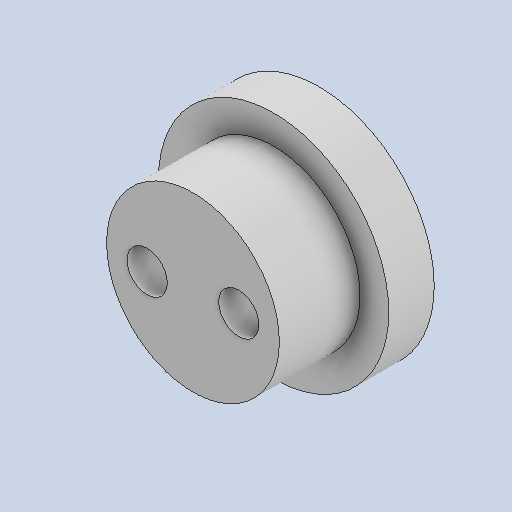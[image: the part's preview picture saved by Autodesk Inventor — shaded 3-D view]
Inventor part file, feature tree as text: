
AUTODESK INVENTOR PART (.ipt)
format: ipt  version: 2023 (Build 270158000, 158)  size: 157,696 bytes
history: native  units: in
note: dims shown in document units (in); Inventor stores cm internally (conversion verified against a paired STEP export)
features: other x3, extrude x2, sketch x2, reference x1
ambient origin geometry x8: Origin, YZ Plane, XZ Plane, XY Plane, X Axis, Y Axis, Z Axis, Center Point
bodies: Solid1 (feature_tree)
feature tree (8):
  extrude  "Extrusion1"  Depth=0.1554in TaperAngle=0.0deg
  extrude  "Extrusion2"  Depth=0.2756in TaperAngle=0.0deg
  sketch  "Sketch1"  dims[d0=0.7874in d1=0.1554in d2=0.0in]
  reference  "Reference1"
  sketch  "Sketch2"  dims[d3=0.5906in d4=0.2756in d5=0.0in d6=0.315in]
  other  "<userpath>\OneDrive\Documents\Robotics Club\Cycloidal Drive\Drive.iam"
  other  "Drive.iam"
  other  "Shaft-3:1"
